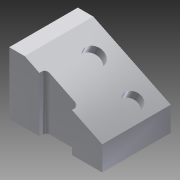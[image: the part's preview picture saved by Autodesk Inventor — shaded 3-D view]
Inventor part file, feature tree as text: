
AUTODESK INVENTOR PART (.ipt)
format: ipt  version: 2015 (Build 190159000, 159)  size: 155,648 bytes
history: native  units: in
note: dims shown in document units (in); Inventor stores cm internally (conversion verified against a paired STEP export)
features: sketch x4, extrude x3, shell x1
ambient origin geometry x8: Origin, YZ Plane, XZ Plane, XY Plane, X Axis, Y Axis, Z Axis, Center Point
bodies: Solid1 (feature_tree)
feature tree (8):
  extrude  "Extrusion1"  TaperAngle=0.0deg  [1 undecoded]
  extrude  "Extrusion2"  TaperAngle=0.0deg  [1 undecoded]
  sketch  "Sketch3"  dims[d19=1.225in d20=0.25in d21=1.1375in d22=0.1458in d23=3.5in d24=0.5833in d25=2.3333in d26=0.0in]
  extrude  "Extrusion3"  Depth=0.3229in
  shell  "Shell1"  Thickness=0.0in
  sketch  "Sketch1"  dims[d5=0.0in d14=0.0in]
  sketch  "Sketch2"  dims[d18=0.1458in]
  sketch  "Sketch4"  dims[d27=0.0in d28=0.3229in d29=0.0in]
note: 2 required parameter values undecoded (feature->parameter linkage not recoverable at this tier; creation-order binding heuristic only, values carry confidence <= 0.55)
